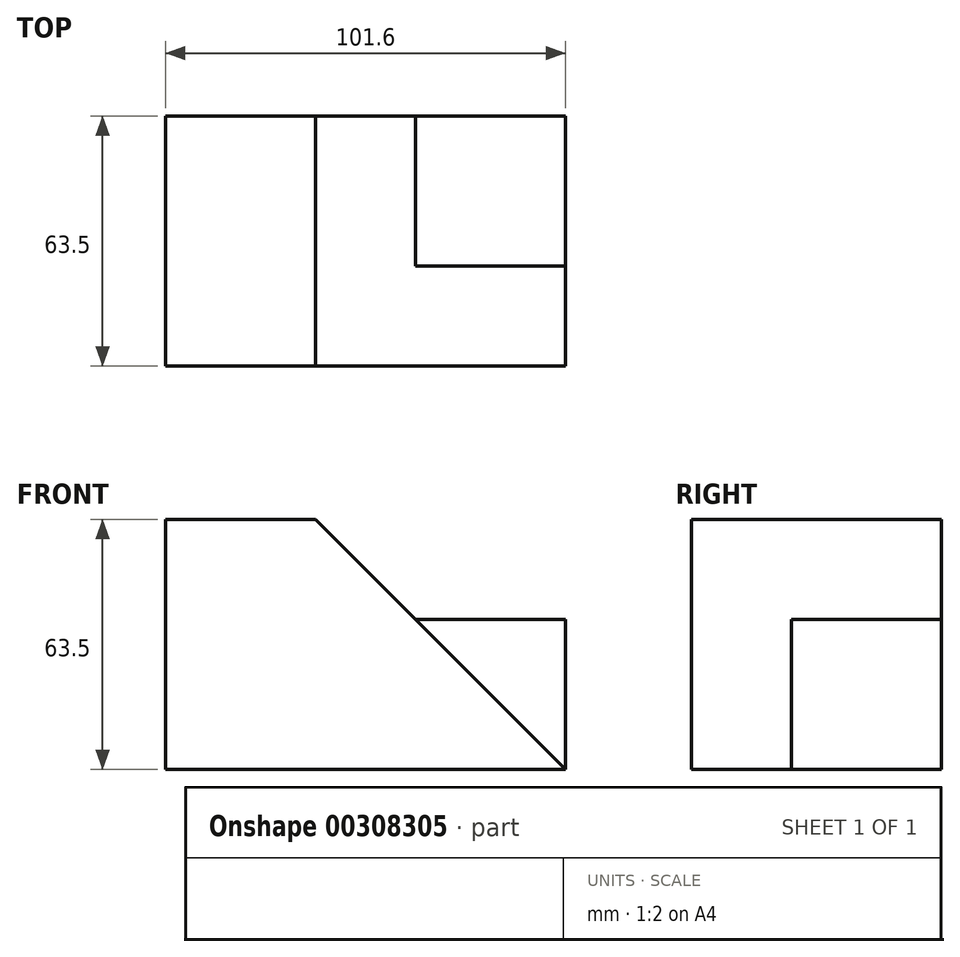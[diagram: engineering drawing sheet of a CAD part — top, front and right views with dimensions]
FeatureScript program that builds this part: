
annotation { "Feature Type Name" : "Feature", "Feature Type Description" : "" }
export const myFeature = defineFeature(function(context is Context, id is Id, definition is map)
    precondition{}
    {
        {
            var Q0;
            Q0=qCreatedBy(makeId("Front.planeOp"),FACE);
            var sketch = newSketch(context, id + "F0", { "sketchPlane" : qUnion([Q0])});
            skLineSegment(sketch, "E0", {"start": v(-27.25, -31.47) * mm, "end": v(74.35, -31.47) * mm});
            skLineSegment(sketch, "E1", {"start": v(-27.25, -31.47) * mm, "end": v(-27.25, 32.03) * mm});
            skLineSegment(sketch, "E2", {"start": v(-27.25, 32.03) * mm, "end": v(10.85, 32.03) * mm});
            skLineSegment(sketch, "E3", {"start": v(10.85, 32.03) * mm, "end": v(74.35, -31.47) * mm});
            skLineSegment(sketch, "E4", {"start": v(74.35, -31.47) * mm, "end": v(74.35, 6.63) * mm});
            skLineSegment(sketch, "E5", {"start": v(74.35, 6.63) * mm, "end": v(36.25, 6.63) * mm});
            skSolve(sketch);
        }
        {
            var Q0;
            Q0=makeQuery(id+"F0.imprint","IMPRINT",FACE,{"disambiguationData":[TD([[makeQuery(id+"F0.imprint","IMPRINT",EDGE,{"derivedFrom":sQuery(id+"F0.wireOp",EDGE,"E0")}),1.0]])]});
            extrude(context, id + "F1", {"entities" : qUnion([Q0]), "depth" : 63.5 * mm});
        }
        {
            var Q0;
            {var subQ0=sQuery(id+"F0.wireOp",EDGE,"E4");Q0=makeQuery(id+"F0.imprint","IMPRINT",FACE,{"disambiguationData":[TD([[makeQuery(id+"F0.imprint","IMPRINT",EDGE,{"derivedFrom":subQ0}),1.0]])]});}
            extrude(context, id + "F2", {"entities" : qUnion([Q0]), "operationType" : NewBodyOperationType.ADD, "depth" : 38.1 * mm});
        }
    });
